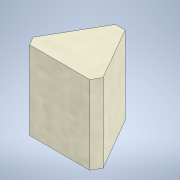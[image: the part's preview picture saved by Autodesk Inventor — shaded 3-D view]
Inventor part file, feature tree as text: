
AUTODESK INVENTOR PART (.ipt)
format: ipt  version: 2021 (Build 250183000, 183)  size: 114,176 bytes
history: native  units: mm
features: extrude x1, sketch x1
ambient origin geometry x8: Origin, YZ Plane, XZ Plane, XY Plane, X Axis, Y Axis, Z Axis, Center Point
bodies: Solid1 (feature_tree)
feature tree (2):
  extrude  "Extrusion1"  Depth=28.25mm
  sketch  "Sketch1"  dims[d0=21.8mm d1=3.464102mm d2=28.25mm d3=0.0mm d4=24.8mm]
